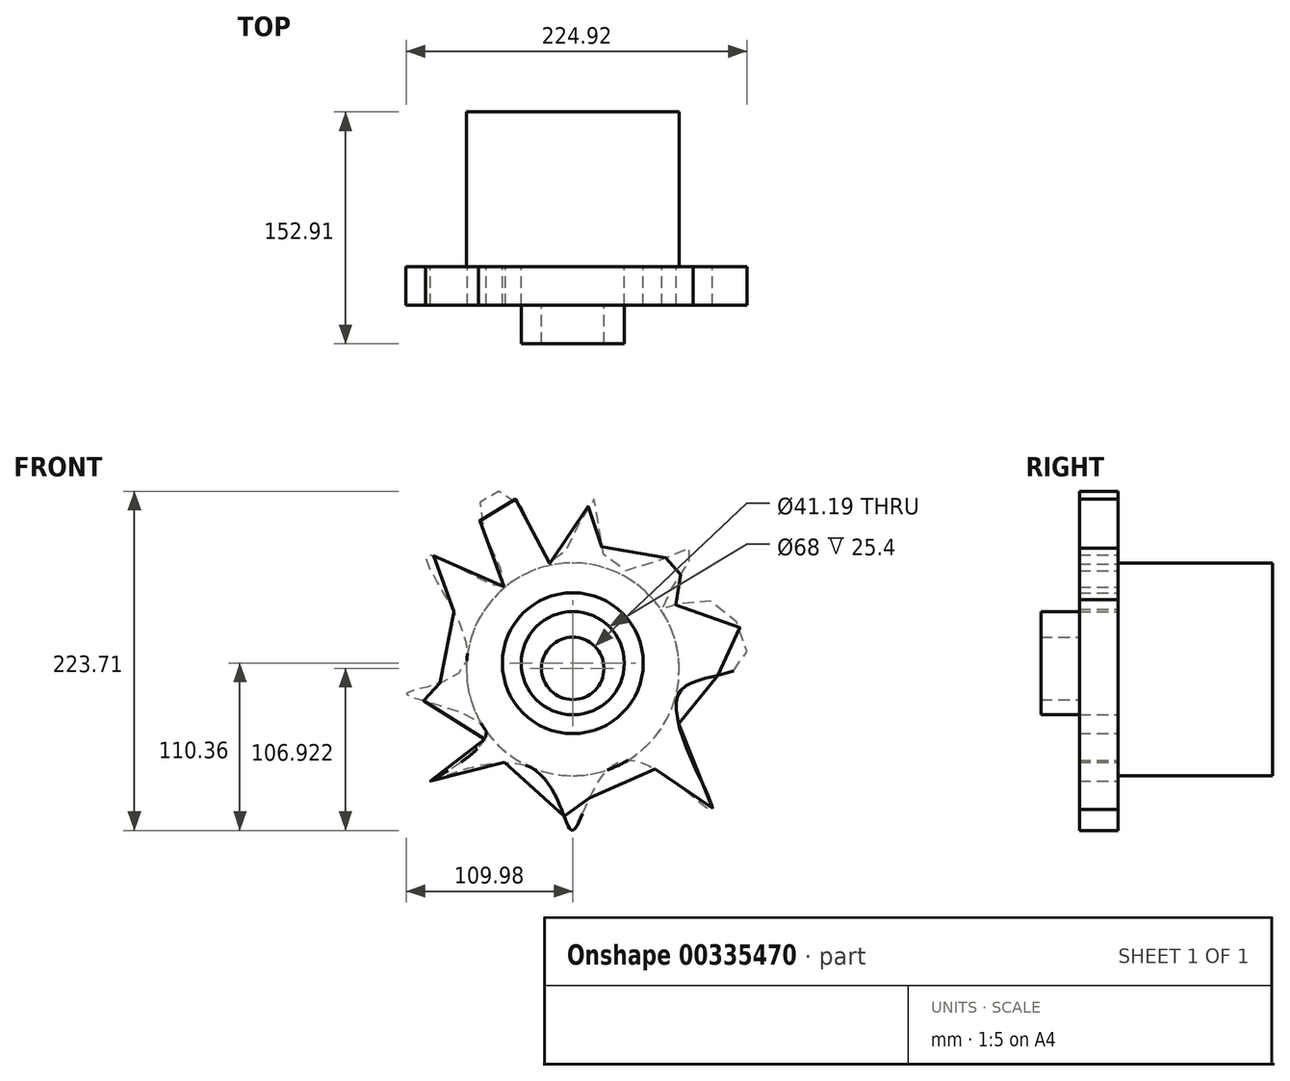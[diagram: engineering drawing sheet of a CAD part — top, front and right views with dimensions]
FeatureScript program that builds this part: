
annotation { "Feature Type Name" : "Feature", "Feature Type Description" : "" }
export const myFeature = defineFeature(function(context is Context, id is Id, definition is map)
    precondition{}
    {
        {
            var Q0;
            Q0=qCreatedBy(makeId("Front.planeOp"),FACE);
            var sketch = newSketch(context, id + "F0", { "sketchPlane" : qUnion([Q0])});
            skCircle(sketch, "E0", {"center": v(0, 0) * mm, "radius": 46.48 * mm});
            skCircle(sketch, "E1", {"center": v(0, 0) * mm, "radius": 34 * mm});
            skSolve(sketch);
        }
        {
            var Q0;
            Q0=makeQuery(id+"F0.imprint","IMPRINT",FACE,{"disambiguationData":[TD([[makeQuery(id+"F0.imprint","IMPRINT",EDGE,{"derivedFrom":sQuery(id+"F0.wireOp",EDGE,"E0")}),1.0]])]});
            extrude(context, id + "F1", {"entities" : qUnion([Q0]), "depth" : 25.4 * mm});
        }
        {
            var Q0;
            Q0=makeQuery(id+"F1.opExtrude","CAP_FACE",FACE,{"disambiguationData":[OSD([sQuery(id+"F0.wireOp",EDGE,"E0"),sQuery(id+"F0.wireOp",EDGE,"E1")])],"isStart":false});
            var sketch = newSketch(context, id + "F2", { "sketchPlane" : qUnion([Q0])});
            skCircle(sketch, "E2", {"center": v(0, -3.44) * mm, "radius": 20.6 * mm});
            skSolve(sketch);
        }
        {
            var Q0;
            Q0 = qSketchRegion(id + "FZzwbaJ4vJ1rLNj_1", true);
            var Q1;
            Q1=makeQuery(id+"F2.imprint","IMPRINT",FACE,{"disambiguationData":[TD([[makeQuery(id+"F2.imprint","IMPRINT",EDGE,{"derivedFrom":sQuery(id+"F2.wireOp",EDGE,"E2")}),-1.0]])]});
            extrude(context, id + "F3", {"entities" : qUnion([Q0, Q1]), "depth" : 25.4 * mm});
        }
        {
            var Q0;
            Q0=qCreatedBy(makeId("Front.planeOp"),FACE);
            var sketch = newSketch(context, id + "F4", { "sketchPlane" : qUnion([Q0])});
            skCircle(sketch, "E3", {"center": v(0, -4.03) * mm, "radius": 70.2 * mm});
            skSolve(sketch);
        }
        {
            var Q0;
            Q0 = qSketchRegion(id + "F4", true);
            extrude(context, id + "F5", {"entities" : qUnion([Q0]), "operationType" : NewBodyOperationType.ADD, "oppositeDirection" : true, "depth" : 57.4 * mm});
        }
        {
            var Q0;
            Q0=qCreatedBy(makeId("Front.planeOp"),FACE);
            var sketch = newSketch(context, id + "F6", { "sketchPlane" : qUnion([Q0])});
            skLineSegment(sketch, "E4.bottom", {"start": v(-94.69, 14.1) * mm, "end": v(-85.77, 14.1) * mm});
            skLineSegment(sketch, "E4.top", {"start": v(-94.69, -19.28) * mm, "end": v(-85.77, -19.28) * mm});
            skLineSegment(sketch, "E4.left", {"start": v(-94.69, 14.1) * mm, "end": v(-94.69, -19.28) * mm});
            skLineSegment(sketch, "E4.right", {"start": v(-85.77, 14.1) * mm, "end": v(-85.77, -19.28) * mm});
            skSolve(sketch);
        }
        {
            var Q0;
            Q0 = qSketchRegion(id + "F6", true);
            extrude(context, id + "F7", {"entities" : qUnion([Q0]), "depth" : 25.4 * mm});
        }
        {
            var Q0;
            Q0=makeQuery(id+"F7.opExtrude","SWEPT_BODY",BODY,{"disambiguationData":[OSD([sQuery(id+"F6.wireOp",EDGE,"E4.bottom"),sQuery(id+"F6.wireOp",EDGE,"E4.top"),sQuery(id+"F6.wireOp",EDGE,"E4.left"),sQuery(id+"F6.wireOp",EDGE,"E4.right")])]});
            deleteBodies(context, id + "F8", {"entities" : qUnion([Q0])});
        }
        {
            var Q0;
            Q0=qCreatedBy(makeId("Front.planeOp"),FACE);
            var sketch = newSketch(context, id + "F9", { "sketchPlane" : qUnion([Q0])});
            skFitSpline(sketch, "E5", {"points": [v(-45.47, 50.37) * mm, v(-96.41, 71.09) * mm, v(-70.51, 0) * mm, v(-109.94, -20.43) * mm, v(-57.27, -44.9) * mm, v(-93.82, -77.7) * mm, v(-28.5, -68.5) * mm, v(0, -110.33) * mm, v(33.1, -64.33) * mm, v(91.81, -96.49) * mm, v(69.07, -22) * mm, v(112.82, 0) * mm, v(88.36, 41.5) * mm, v(58.71, 36.6) * mm, v(79.15, 75.3) * mm, v(27.05, 62.67) * mm, v(14.1, 108.26) * mm, v(-12.66, 65.52) * mm, v(-38.57, 109.07) * mm, v(-62.17, 102.56) * mm, v(-45.47, 50.37) * mm]});
            skSolve(sketch);
        }
        {
            var Q0;
            Q0=makeQuery(id+"F5.opExtrude","CAP_FACE",FACE,{"disambiguationData":[OSD([sQuery(id+"F4.wireOp",EDGE,"E3")])],"isStart":false});
            var Q1;
            Q1=makeQuery(id+"F1.opExtrude","CAP_FACE",FACE,{"disambiguationData":[OSD([sQuery(id+"F0.wireOp",EDGE,"E0"),sQuery(id+"F0.wireOp",EDGE,"E1")])],"isStart":false});
            extrude(context, id + "F10", {"entities" : qUnion([Q0, Q1]), "operationType" : NewBodyOperationType.ADD, "depth" : 44.7 * mm});
        }
        {
            var Q0;
            Q0=makeQuery(id+"F9.imprint","IMPRINT",FACE,{"disambiguationData":[TD([[makeQuery(id+"F9.imprint","IMPRINT",EDGE,{"derivedFrom":sQuery(id+"F9.wireOp",EDGE,"E5")}),1.0]])]});
            extrude(context, id + "F11", {"entities" : qUnion([Q0]), "depth" : 25.4 * mm});
        }
    });
